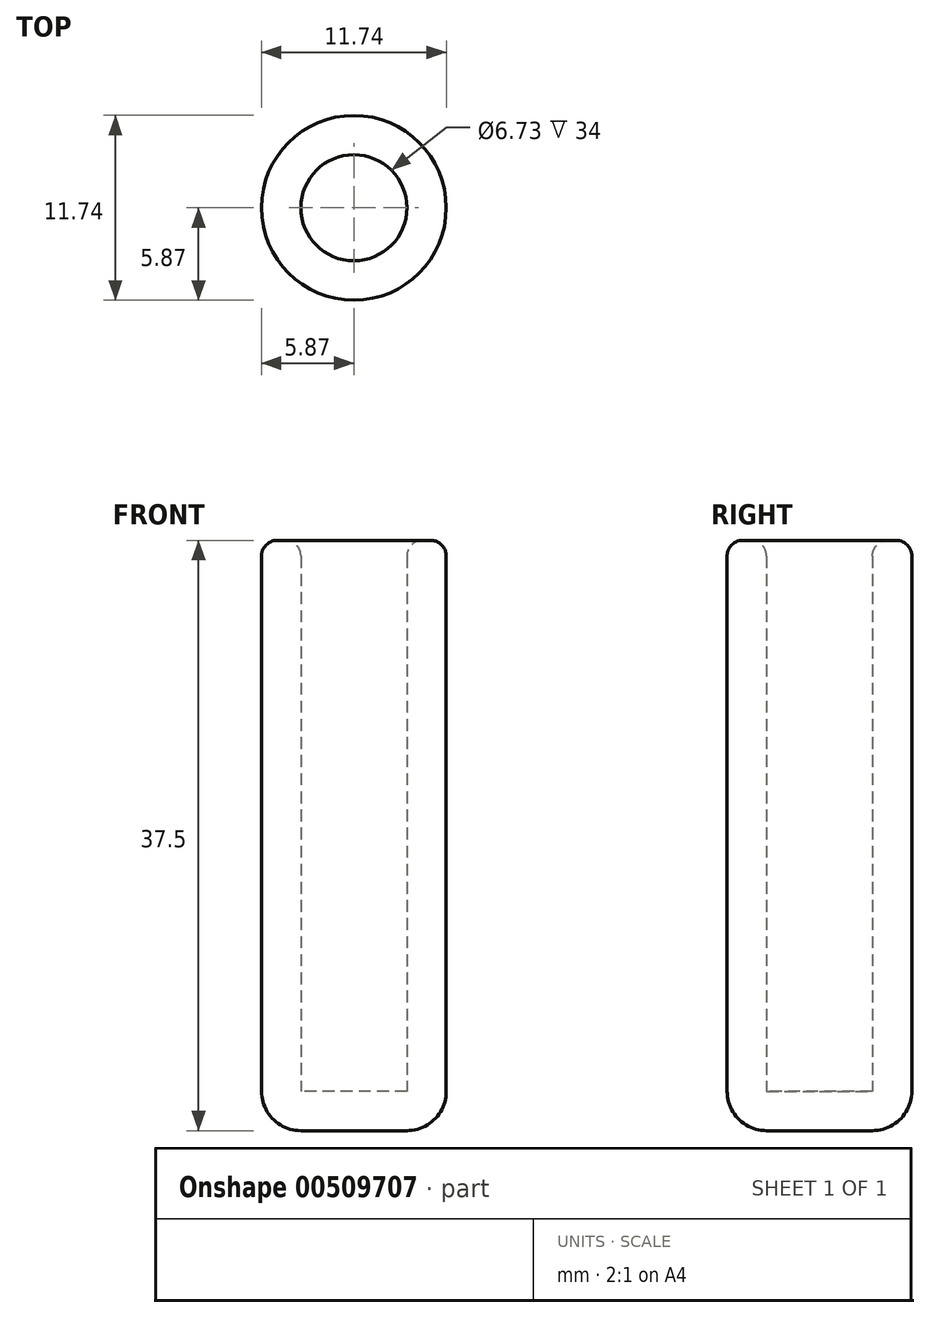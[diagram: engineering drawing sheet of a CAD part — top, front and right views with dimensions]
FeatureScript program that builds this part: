
annotation { "Feature Type Name" : "Feature", "Feature Type Description" : "" }
export const myFeature = defineFeature(function(context is Context, id is Id, definition is map)
    precondition{}
    {
        {
            var Q0;
            Q0=qCreatedBy(makeId("Top.planeOp"),FACE);
            var sketch = newSketch(context, id + "F0", { "sketchPlane" : qUnion([Q0])});
            skCircle(sketch, "E0", {"center": v(0, 0) * mm, "radius": 5.87 * mm});
            skSolve(sketch);
        }
        {
            var Q0;
            Q0=makeQuery(id+"F0.imprint","IMPRINT",FACE,{"disambiguationData":[TD([[makeQuery(id+"F0.imprint","IMPRINT",EDGE,{"derivedFrom":sQuery(id+"F0.wireOp",EDGE,"E0")}),1.0]])]});
            extrude(context, id + "F1", {"entities" : qUnion([Q0]), "depth" : 37.5 * mm});
        }
        {
            var Q0;
            Q0=makeQuery(id+"F1.opExtrude","CAP_FACE",FACE,{"disambiguationData":[OSD([sQuery(id+"F0.wireOp",EDGE,"E0")])],"isStart":false});
            shell(context, id + "F2", {"entities" : qUnion([Q0]), "thickness" : 2.5 * mm});
        }
        {
            var Q0;
            Q0=makeQuery(id+"F1.opExtrude","CAP_EDGE",EDGE,{"disambiguationData":[OSD([sQuery(id+"F0.wireOp",EDGE,"E0")])],"isStart":true});
            fillet(context, id + "F3", {"entities" : qUnion([Q0]), "radius" : 2.5 * mm, "tangentPropagation" : true, "allowEdgeOverflow" : false});
        }
        {
            var Q0;
            Q0=makeQuery(id+"F1.opExtrude","CAP_FACE",FACE,{"disambiguationData":[OSD([sQuery(id+"F0.wireOp",EDGE,"E0")])],"isStart":false});
            var Q1;
            Q1=makeQuery(id+"F1.opExtrude","CAP_EDGE",EDGE,{"disambiguationData":[OSD([sQuery(id+"F0.wireOp",EDGE,"E0")])],"isStart":false});
            fillet(context, id + "F4", {"entities" : qUnion([Q0, Q1]), "radius" : 1 * mm, "tangentPropagation" : true, "allowEdgeOverflow" : false});
        }
    });
